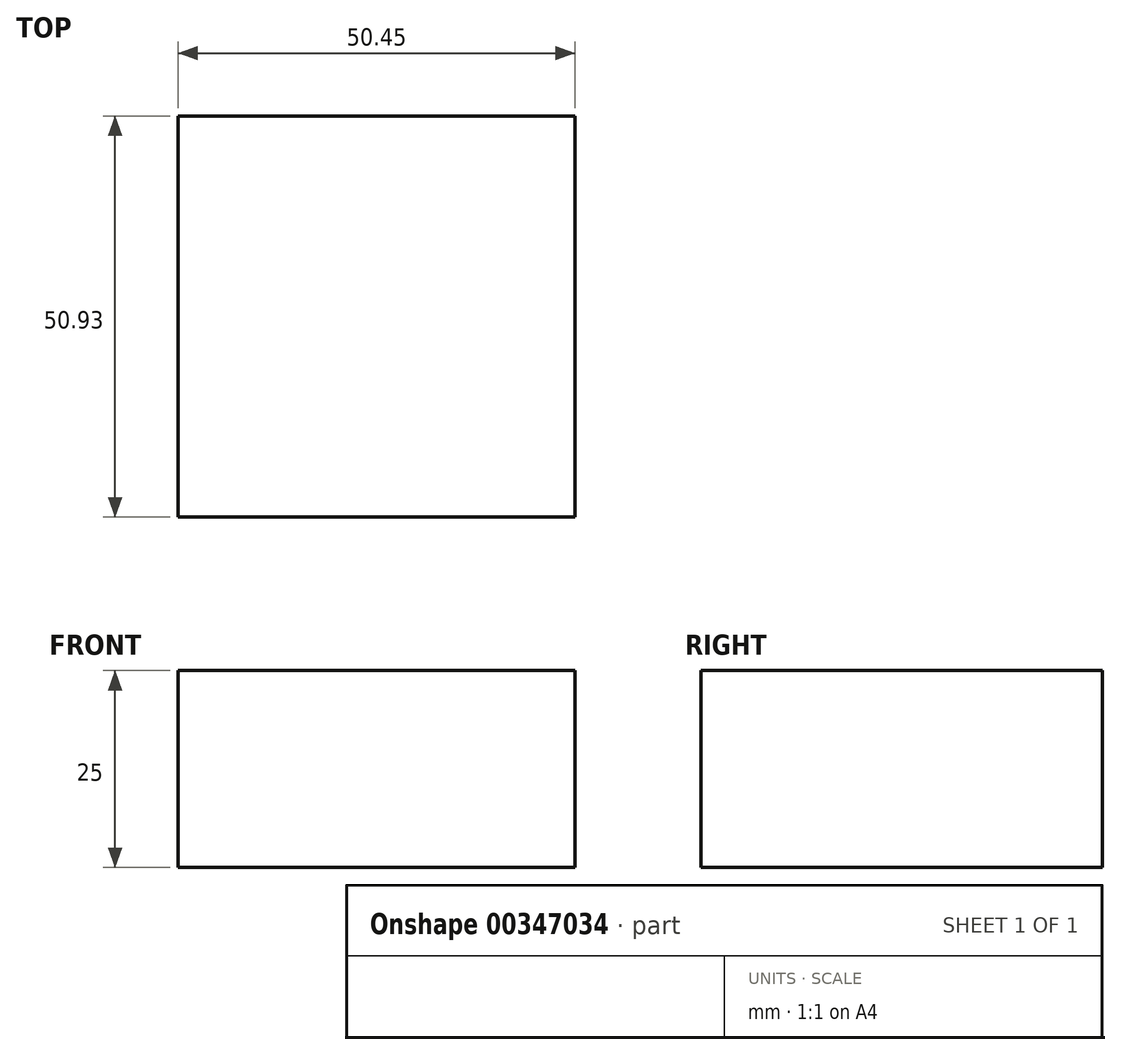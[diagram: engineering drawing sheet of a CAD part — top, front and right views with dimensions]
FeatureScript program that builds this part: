
annotation { "Feature Type Name" : "Feature", "Feature Type Description" : "" }
export const myFeature = defineFeature(function(context is Context, id is Id, definition is map)
    precondition{}
    {
        {
            var Q0;
            Q0=qCreatedBy(makeId("Top.planeOp"),FACE);
            var sketch = newSketch(context, id + "F0", { "sketchPlane" : qUnion([Q0])});
            skLineSegment(sketch, "E0.bottom", {"start": v(0, 0) * mm, "end": v(-50.45, 0) * mm});
            skLineSegment(sketch, "E0.top", {"start": v(0, 50.93) * mm, "end": v(-50.45, 50.93) * mm});
            skLineSegment(sketch, "E0.left", {"start": v(0, 0) * mm, "end": v(0, 50.93) * mm});
            skLineSegment(sketch, "E0.right", {"start": v(-50.45, 0) * mm, "end": v(-50.45, 50.93) * mm});
            skSolve(sketch);
        }
        {
            var Q0;
            Q0=makeQuery(id+"F0.imprint","IMPRINT",FACE,{"disambiguationData":[TD([[makeQuery(id+"F0.imprint","IMPRINT",EDGE,{"derivedFrom":sQuery(id+"F0.wireOp",EDGE,"E0.bottom")}),-1.0]])]});
            extrude(context, id + "F1", {"entities" : qUnion([Q0]), "depth" : 25 * mm});
        }
    });
